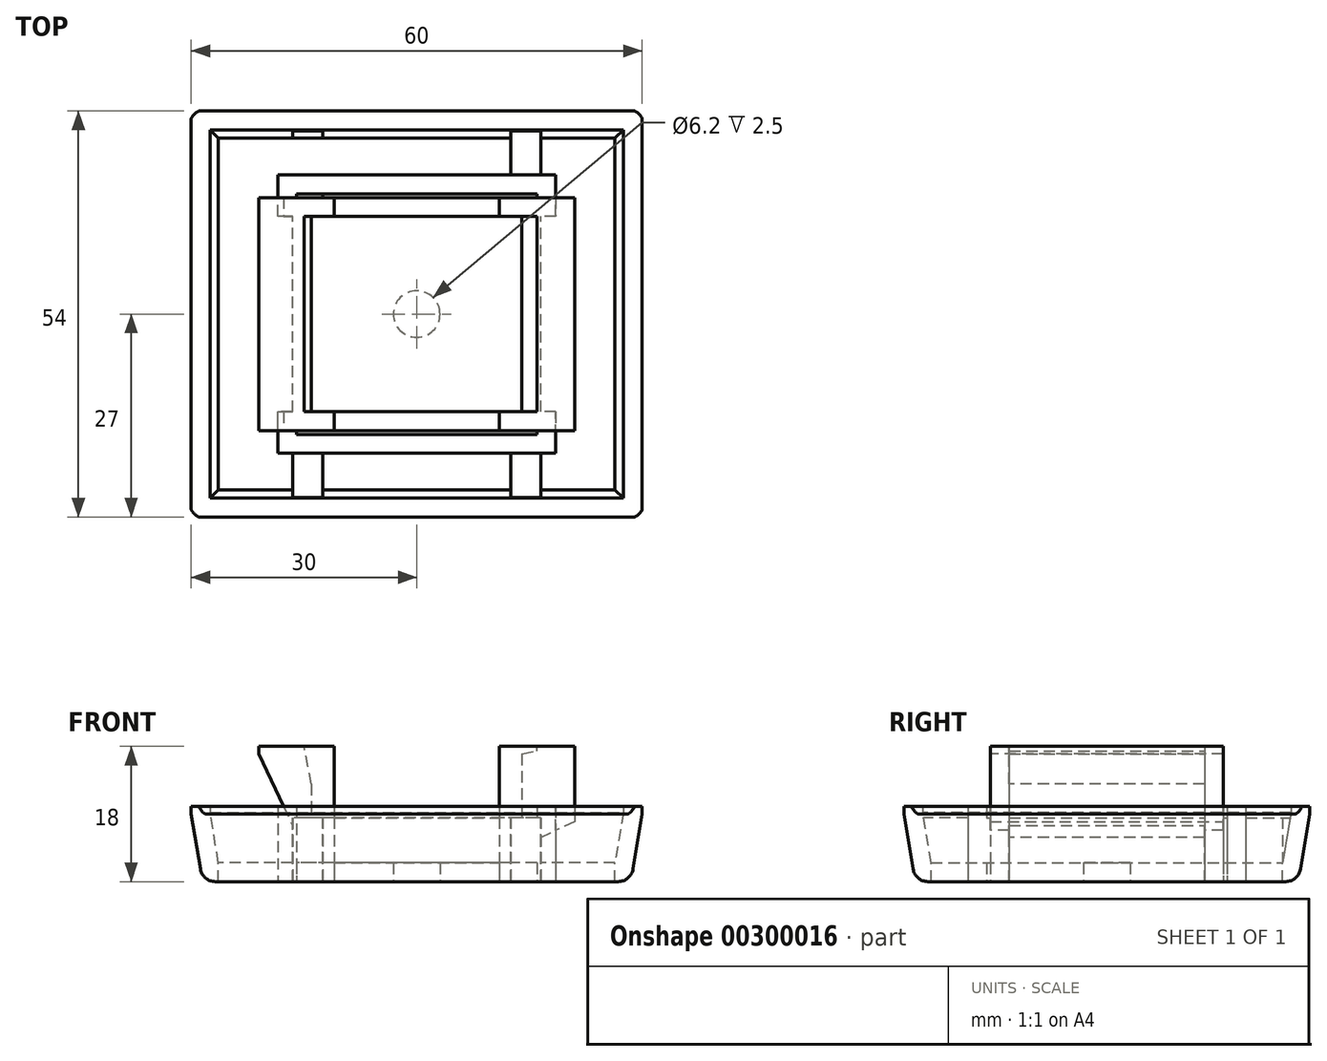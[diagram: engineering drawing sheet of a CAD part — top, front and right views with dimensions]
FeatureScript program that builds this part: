
annotation { "Feature Type Name" : "Feature", "Feature Type Description" : "" }
export const myFeature = defineFeature(function(context is Context, id is Id, definition is map)
    precondition{}
    {
        {
            var Q0;
            Q0=qCreatedBy(makeId("Top.planeOp"),FACE);
            var sketch = newSketch(context, id + "F0", { "sketchPlane" : qUnion([Q0])});
            skLineSegment(sketch, "E0.bottom", {"start": v(30, -27) * mm, "end": v(-30, -27) * mm});
            skLineSegment(sketch, "E0.top", {"start": v(30, 27) * mm, "end": v(-30, 27) * mm});
            skLineSegment(sketch, "E0.left", {"start": v(30, -27) * mm, "end": v(30, 27) * mm});
            skLineSegment(sketch, "E0.right", {"start": v(-30, -27) * mm, "end": v(-30, 27) * mm});
            skPoint(sketch, "E0.middle", {"position": v(0, 0) * mm});
            skLineSegment(sketch, "E1.bottom", {"start": v(21, -15.5) * mm, "end": v(-21, -15.5) * mm});
            skLineSegment(sketch, "E1.top", {"start": v(21, 15.5) * mm, "end": v(-21, 15.5) * mm});
            skLineSegment(sketch, "E1.left", {"start": v(21, -15.5) * mm, "end": v(21, 15.5) * mm});
            skLineSegment(sketch, "E1.right", {"start": v(-21, -15.5) * mm, "end": v(-21, 15.5) * mm});
            skCircle(sketch, "E2", {"center": v(0, 0) * mm, "radius": 3.1 * mm});
            skLineSegment(sketch, "E3.bottom", {"start": v(11, -15.5) * mm, "end": v(-11, -15.5) * mm});
            skLineSegment(sketch, "E3.top", {"start": v(11, 15.5) * mm, "end": v(-11, 15.5) * mm});
            skLineSegment(sketch, "E3.left", {"start": v(11, -15.5) * mm, "end": v(11, 15.5) * mm});
            skLineSegment(sketch, "E3.right", {"start": v(-11, -15.5) * mm, "end": v(-11, 15.5) * mm});
            skLineSegment(sketch, "E4.bottom", {"start": v(14, -13) * mm, "end": v(-14, -13) * mm});
            skLineSegment(sketch, "E4.top", {"start": v(14, 13) * mm, "end": v(-14, 13) * mm});
            skLineSegment(sketch, "E4.left", {"start": v(14, -13) * mm, "end": v(14, 13) * mm});
            skLineSegment(sketch, "E4.right", {"start": v(-14, -13) * mm, "end": v(-14, 13) * mm});
            skLineSegment(sketch, "E5.bottom", {"start": v(16, -16) * mm, "end": v(-16, -16) * mm});
            skLineSegment(sketch, "E5.top", {"start": v(16, 16) * mm, "end": v(-16, 16) * mm});
            skLineSegment(sketch, "E5.left", {"start": v(16, -16) * mm, "end": v(16, 16) * mm});
            skLineSegment(sketch, "E5.right", {"start": v(-16, -16) * mm, "end": v(-16, 16) * mm});
            skSolve(sketch);
        }
        {
            var Q0;
            Q0=makeQuery(id+"F0.imprint","IMPRINT",FACE,{"disambiguationData":[TD([[makeQuery(id+"F0.imprint","IMPRINT",EDGE,{"derivedFrom":sQuery(id+"F0.wireOp",EDGE,"E0.bottom")}),-1.0]])]});
            var Q1;
            {var subQ0=sQuery(id+"F0.wireOp",EDGE,"E3.top");Q1=makeQuery(id+"F0.imprint","IMPRINT",FACE,{"disambiguationData":[TD([[makeQuery(id+"F0.imprint","IMPRINT",EDGE,{"derivedFrom":subQ0}),1.0]])]});}
            var Q2;
            {var subQ0=sQuery(id+"F0.wireOp",EDGE,"E3.bottom");Q2=makeQuery(id+"F0.imprint","IMPRINT",FACE,{"disambiguationData":[TD([[makeQuery(id+"F0.imprint","IMPRINT",EDGE,{"derivedFrom":subQ0}),-1.0]])]});}
            var Q3;
            {var subQ0=sQuery(id+"F0.wireOp",EDGE,"E1.right");Q3=makeQuery(id+"F0.imprint","IMPRINT",FACE,{"disambiguationData":[TD([[makeQuery(id+"F0.imprint","IMPRINT",EDGE,{"derivedFrom":subQ0}),-1.0]])]});}
            var Q4;
            {var subQ0=sQuery(id+"F0.wireOp",EDGE,"E1.left");Q4=makeQuery(id+"F0.imprint","IMPRINT",FACE,{"disambiguationData":[TD([[makeQuery(id+"F0.imprint","IMPRINT",EDGE,{"derivedFrom":subQ0}),1.0]])]});}
            var Q5;
            {var subQ1=sQuery(id+"F0.wireOp",EDGE,"E3.bottom");Q5=makeQuery(id+"F0.imprint","IMPRINT",FACE,{"disambiguationData":[TD([[makeQuery(id+"F0.imprint","IMPRINT",EDGE,{"derivedFrom":subQ1}),1.0]])]});}
            var Q6;
            {var subQ1=sQuery(id+"F0.wireOp",EDGE,"E3.top");Q6=makeQuery(id+"F0.imprint","IMPRINT",FACE,{"disambiguationData":[TD([[makeQuery(id+"F0.imprint","IMPRINT",EDGE,{"derivedFrom":subQ1}),-1.0]])]});}
            extrude(context, id + "F1", {"entities" : qUnion([Q0, Q1, Q2, Q3, Q4, Q5, Q6]), "depth" : 10 * mm});
        }
        {
            var Q0;
            Q0=makeQuery(id+"F0.imprint","IMPRINT",FACE,{"disambiguationData":[TD([[makeQuery(id+"F0.imprint","IMPRINT",EDGE,{"derivedFrom":sQuery(id+"F0.wireOp",EDGE,"E2")}),-1.0]])]});
            var Q1;
            {var subQ5=sQuery(id+"F0.wireOp",EDGE,"E4.right");Q1=makeQuery(id+"F0.imprint","IMPRINT",FACE,{"disambiguationData":[TD([[makeQuery(id+"F0.imprint","IMPRINT",EDGE,{"derivedFrom":subQ5}),-1.0]])]});}
            var Q2;
            {var subQ5=sQuery(id+"F0.wireOp",EDGE,"E4.left");Q2=makeQuery(id+"F0.imprint","IMPRINT",FACE,{"disambiguationData":[TD([[makeQuery(id+"F0.imprint","IMPRINT",EDGE,{"derivedFrom":subQ5}),1.0]])]});}
            extrude(context, id + "F2", {"entities" : qUnion([Q0, Q1, Q2]), "operationType" : NewBodyOperationType.ADD, "depth" : 5 * mm});
        }
        {
            var Q0;
            Q0=makeQuery(id+"F1.opExtrude","CAP_EDGE",EDGE,{"disambiguationData":[OSD([sQuery(id+"F0.wireOp",EDGE,"E0.right")])],"isStart":true});
            var Q1;
            Q1=makeQuery(id+"F1.opExtrude","CAP_EDGE",EDGE,{"disambiguationData":[OSD([sQuery(id+"F0.wireOp",EDGE,"E0.bottom")])],"isStart":true});
            var Q2;
            Q2=makeQuery(id+"F1.opExtrude","CAP_EDGE",EDGE,{"disambiguationData":[OSD([sQuery(id+"F0.wireOp",EDGE,"E0.left")])],"isStart":true});
            var Q3;
            Q3=makeQuery(id+"F1.opExtrude","CAP_EDGE",EDGE,{"disambiguationData":[OSD([sQuery(id+"F0.wireOp",EDGE,"E0.top")])],"isStart":true});
            chamfer(context, id + "F3", {"entities" : qUnion([Q0, Q1, Q2, Q3]), "chamferType" : ChamferType.TWO_OFFSETS, "width1" : 1.5 * mm, "oppositeDirection" : false, "width2" : 9 * mm, "tangentPropagation" : true});
        }
        {
            var Q0;
            {var subQ12=sQuery(id+"F0.wireOp",EDGE,"E4.right");Q0=makeQuery(id+"F0.imprint","IMPRINT",FACE,{"disambiguationData":[TD([[makeQuery(id+"F0.imprint","IMPRINT",EDGE,{"derivedFrom":subQ12}),1.0]])]});}
            var Q1;
            {var subQ12=sQuery(id+"F0.wireOp",EDGE,"E4.left");Q1=makeQuery(id+"F0.imprint","IMPRINT",FACE,{"disambiguationData":[TD([[makeQuery(id+"F0.imprint","IMPRINT",EDGE,{"derivedFrom":subQ12}),-1.0]])]});}
            extrude(context, id + "F4", {"entities" : qUnion([Q0, Q1]), "operationType" : NewBodyOperationType.ADD, "depth" : 18 * mm});
        }
        {
            var Q0;
            Q0=makeQuery(id+"F4.opExtrude","CAP_EDGE",EDGE,{"disambiguationData":[OSD([sQuery(id+"F0.wireOp",EDGE,"E4.right")])],"isStart":false});
            chamfer(context, id + "F5", {"entities" : qUnion([Q0]), "chamferType" : ChamferType.TWO_OFFSETS, "width1" : 1 * mm, "oppositeDirection" : false, "width2" : 5 * mm, "tangentPropagation" : true});
        }
        {
            var Q0;
            Q0=makeQuery(id+"F4.opExtrude","CAP_EDGE",EDGE,{"disambiguationData":[OSD([sQuery(id+"F0.wireOp",EDGE,"E4.left")])],"isStart":false});
            chamfer(context, id + "F6", {"entities" : qUnion([Q0]), "chamferType" : ChamferType.TWO_OFFSETS, "width1" : 5 * mm, "oppositeDirection" : false, "width2" : 1 * mm, "tangentPropagation" : true});
        }
        {
            var Q0;
            {var subQ0=sQuery(id+"F0.wireOp",EDGE,"E1.right");Q0=makeQuery(id+"F0.imprint","IMPRINT",FACE,{"disambiguationData":[TD([[makeQuery(id+"F0.imprint","IMPRINT",EDGE,{"derivedFrom":subQ0}),-1.0]])]});}
            var Q1;
            {var subQ0=sQuery(id+"F0.wireOp",EDGE,"E1.left");Q1=makeQuery(id+"F0.imprint","IMPRINT",FACE,{"disambiguationData":[TD([[makeQuery(id+"F0.imprint","IMPRINT",EDGE,{"derivedFrom":subQ0}),1.0]])]});}
            extrude(context, id + "F7", {"entities" : qUnion([Q0, Q1]), "depth" : 18 * mm});
        }
        {
            var Q0;
            Q0=makeQuery(id+"F7.opExtrude","CAP_EDGE",EDGE,{"disambiguationData":[OSD([sQuery(id+"F0.wireOp",EDGE,"E1.right")])],"isStart":true});
            chamfer(context, id + "F8", {"entities" : qUnion([Q0]), "chamferType" : ChamferType.TWO_OFFSETS, "width1" : 8 * mm, "oppositeDirection" : false, "width2" : 17 * mm, "tangentPropagation" : true});
        }
        {
            var Q0;
            Q0=makeQuery(id+"F7.opExtrude","CAP_EDGE",EDGE,{"disambiguationData":[OSD([sQuery(id+"F0.wireOp",EDGE,"E1.left")])],"isStart":true});
            chamfer(context, id + "F9", {"entities" : qUnion([Q0]), "chamferType" : ChamferType.TWO_OFFSETS, "width1" : 8 * mm, "oppositeDirection" : true, "width2" : 17 * mm, "tangentPropagation" : true});
        }
        {
            var Q0;
            Q0=makeQuery(id+"F1.opExtrude","CAP_FACE",FACE,{"disambiguationData":[OSD([sQuery(id+"F0.wireOp",EDGE,"E0.bottom"),sQuery(id+"F0.wireOp",EDGE,"E0.top"),sQuery(id+"F0.wireOp",EDGE,"E0.left"),sQuery(id+"F0.wireOp",EDGE,"E0.right"),sQuery(id+"F0.wireOp",EDGE,"E1.bottom"),sQuery(id+"F0.wireOp",EDGE,"E1.top"),sQuery(id+"F0.wireOp",EDGE,"E3.left"),sQuery(id+"F0.wireOp",EDGE,"E3.right"),sQuery(id+"F0.wireOp",EDGE,"E4.bottom"),sQuery(id+"F0.wireOp",EDGE,"E4.top"),sQuery(id+"F0.wireOp",EDGE,"E5.left"),sQuery(id+"F0.wireOp",EDGE,"E5.right")])],"isStart":false});
            shell(context, id + "F10", {"entities" : qUnion([Q0]), "thickness" : 2.5 * mm});
        }
        {
            var Q0;
            Q0=makeQuery(id+"F3.opChamfer","BLEND_EDGE",EDGE,{"blendedFrom":[makeQuery(id+"F1.opExtrude","CAP_EDGE",EDGE,{"disambiguationData":[OSD([sQuery(id+"F0.wireOp",EDGE,"E0.bottom")])],"isStart":true}),makeQuery(id+"F1.opExtrude","CAP_EDGE",EDGE,{"disambiguationData":[OSD([sQuery(id+"F0.wireOp",EDGE,"E0.right")])],"isStart":true})],"blendedInto":[]});
            var Q1;
            Q1=makeQuery(id+"F3.opChamfer","BLEND_EDGE",EDGE,{"blendedFrom":[makeQuery(id+"F1.opExtrude","CAP_EDGE",EDGE,{"disambiguationData":[OSD([sQuery(id+"F0.wireOp",EDGE,"E0.top")])],"isStart":true}),makeQuery(id+"F1.opExtrude","CAP_EDGE",EDGE,{"disambiguationData":[OSD([sQuery(id+"F0.wireOp",EDGE,"E0.right")])],"isStart":true})],"blendedInto":[]});
            var Q2;
            Q2=makeQuery(id+"F3.opChamfer","BLEND_EDGE",EDGE,{"blendedFrom":[makeQuery(id+"F1.opExtrude","CAP_EDGE",EDGE,{"disambiguationData":[OSD([sQuery(id+"F0.wireOp",EDGE,"E0.top")])],"isStart":true}),makeQuery(id+"F1.opExtrude","CAP_EDGE",EDGE,{"disambiguationData":[OSD([sQuery(id+"F0.wireOp",EDGE,"E0.left")])],"isStart":true})],"blendedInto":[]});
            var Q3;
            Q3=makeQuery(id+"F3.opChamfer","BLEND_EDGE",EDGE,{"blendedFrom":[makeQuery(id+"F1.opExtrude","CAP_EDGE",EDGE,{"disambiguationData":[OSD([sQuery(id+"F0.wireOp",EDGE,"E0.bottom")])],"isStart":true}),makeQuery(id+"F1.opExtrude","CAP_EDGE",EDGE,{"disambiguationData":[OSD([sQuery(id+"F0.wireOp",EDGE,"E0.left")])],"isStart":true})],"blendedInto":[]});
            var Q4;
            {var subQ0=sQuery(id+"F0.wireOp",EDGE,"E4.top");var subQ1=sQuery(id+"F0.wireOp",EDGE,"E4.bottom");var subQ2=sQuery(id+"F0.wireOp",EDGE,"E0.left");Q4=makeQuery(id+"F3.opChamfer","BLEND_EDGE",EDGE,{"blendedFrom":[makeQuery(id+"F1.opExtrude","CAP_EDGE",EDGE,{"disambiguationData":[OSD([subQ2])],"isStart":true}),makeQuery(id+"F2.boolean.opBoolean","MERGE",FACE,{"derivedFrom":[makeQuery(id+"F1.opExtrude","CAP_FACE",FACE,{"disambiguationData":[OSD([sQuery(id+"F0.wireOp",EDGE,"E0.bottom"),sQuery(id+"F0.wireOp",EDGE,"E0.top"),subQ2,sQuery(id+"F0.wireOp",EDGE,"E0.right"),sQuery(id+"F0.wireOp",EDGE,"E1.bottom"),sQuery(id+"F0.wireOp",EDGE,"E1.top"),sQuery(id+"F0.wireOp",EDGE,"E3.left"),sQuery(id+"F0.wireOp",EDGE,"E3.right"),subQ1,subQ0,sQuery(id+"F0.wireOp",EDGE,"E5.left"),sQuery(id+"F0.wireOp",EDGE,"E5.right")])],"isStart":true}),makeQuery(id+"F2.opExtrude","CAP_FACE",FACE,{"disambiguationData":[OSD([sQuery(id+"F0.wireOp",EDGE,"E2"),subQ1,subQ0,sQuery(id+"F0.wireOp",EDGE,"E4.left"),sQuery(id+"F0.wireOp",EDGE,"E4.right")])],"isStart":true})]})],"blendedInto":[makeQuery(id+"F2.boolean.opBoolean","MERGE",FACE,{"derivedFrom":[makeQuery(id+"F1.opExtrude","CAP_FACE",FACE,{"disambiguationData":[OSD([sQuery(id+"F0.wireOp",EDGE,"E0.bottom"),sQuery(id+"F0.wireOp",EDGE,"E0.top"),subQ2,sQuery(id+"F0.wireOp",EDGE,"E0.right"),sQuery(id+"F0.wireOp",EDGE,"E1.bottom"),sQuery(id+"F0.wireOp",EDGE,"E1.top"),sQuery(id+"F0.wireOp",EDGE,"E3.left"),sQuery(id+"F0.wireOp",EDGE,"E3.right"),subQ1,subQ0,sQuery(id+"F0.wireOp",EDGE,"E5.left"),sQuery(id+"F0.wireOp",EDGE,"E5.right")])],"isStart":true}),makeQuery(id+"F2.opExtrude","CAP_FACE",FACE,{"disambiguationData":[OSD([sQuery(id+"F0.wireOp",EDGE,"E2"),subQ1,subQ0,sQuery(id+"F0.wireOp",EDGE,"E4.left"),sQuery(id+"F0.wireOp",EDGE,"E4.right")])],"isStart":true})]})]});}
            var Q5;
            {var subQ0=sQuery(id+"F0.wireOp",EDGE,"E4.top");var subQ1=sQuery(id+"F0.wireOp",EDGE,"E4.bottom");var subQ2=sQuery(id+"F0.wireOp",EDGE,"E0.bottom");Q5=makeQuery(id+"F3.opChamfer","BLEND_EDGE",EDGE,{"blendedFrom":[makeQuery(id+"F1.opExtrude","CAP_EDGE",EDGE,{"disambiguationData":[OSD([subQ2])],"isStart":true}),makeQuery(id+"F2.boolean.opBoolean","MERGE",FACE,{"derivedFrom":[makeQuery(id+"F1.opExtrude","CAP_FACE",FACE,{"disambiguationData":[OSD([subQ2,sQuery(id+"F0.wireOp",EDGE,"E0.top"),sQuery(id+"F0.wireOp",EDGE,"E0.left"),sQuery(id+"F0.wireOp",EDGE,"E0.right"),sQuery(id+"F0.wireOp",EDGE,"E1.bottom"),sQuery(id+"F0.wireOp",EDGE,"E1.top"),sQuery(id+"F0.wireOp",EDGE,"E3.left"),sQuery(id+"F0.wireOp",EDGE,"E3.right"),subQ1,subQ0,sQuery(id+"F0.wireOp",EDGE,"E5.left"),sQuery(id+"F0.wireOp",EDGE,"E5.right")])],"isStart":true}),makeQuery(id+"F2.opExtrude","CAP_FACE",FACE,{"disambiguationData":[OSD([sQuery(id+"F0.wireOp",EDGE,"E2"),subQ1,subQ0,sQuery(id+"F0.wireOp",EDGE,"E4.left"),sQuery(id+"F0.wireOp",EDGE,"E4.right")])],"isStart":true})]})],"blendedInto":[makeQuery(id+"F2.boolean.opBoolean","MERGE",FACE,{"derivedFrom":[makeQuery(id+"F1.opExtrude","CAP_FACE",FACE,{"disambiguationData":[OSD([subQ2,sQuery(id+"F0.wireOp",EDGE,"E0.top"),sQuery(id+"F0.wireOp",EDGE,"E0.left"),sQuery(id+"F0.wireOp",EDGE,"E0.right"),sQuery(id+"F0.wireOp",EDGE,"E1.bottom"),sQuery(id+"F0.wireOp",EDGE,"E1.top"),sQuery(id+"F0.wireOp",EDGE,"E3.left"),sQuery(id+"F0.wireOp",EDGE,"E3.right"),subQ1,subQ0,sQuery(id+"F0.wireOp",EDGE,"E5.left"),sQuery(id+"F0.wireOp",EDGE,"E5.right")])],"isStart":true}),makeQuery(id+"F2.opExtrude","CAP_FACE",FACE,{"disambiguationData":[OSD([sQuery(id+"F0.wireOp",EDGE,"E2"),subQ1,subQ0,sQuery(id+"F0.wireOp",EDGE,"E4.left"),sQuery(id+"F0.wireOp",EDGE,"E4.right")])],"isStart":true})]})]});}
            var Q6;
            {var subQ0=sQuery(id+"F0.wireOp",EDGE,"E4.top");var subQ1=sQuery(id+"F0.wireOp",EDGE,"E4.bottom");var subQ2=sQuery(id+"F0.wireOp",EDGE,"E0.right");Q6=makeQuery(id+"F3.opChamfer","BLEND_EDGE",EDGE,{"blendedFrom":[makeQuery(id+"F1.opExtrude","CAP_EDGE",EDGE,{"disambiguationData":[OSD([subQ2])],"isStart":true}),makeQuery(id+"F2.boolean.opBoolean","MERGE",FACE,{"derivedFrom":[makeQuery(id+"F1.opExtrude","CAP_FACE",FACE,{"disambiguationData":[OSD([sQuery(id+"F0.wireOp",EDGE,"E0.bottom"),sQuery(id+"F0.wireOp",EDGE,"E0.top"),sQuery(id+"F0.wireOp",EDGE,"E0.left"),subQ2,sQuery(id+"F0.wireOp",EDGE,"E1.bottom"),sQuery(id+"F0.wireOp",EDGE,"E1.top"),sQuery(id+"F0.wireOp",EDGE,"E3.left"),sQuery(id+"F0.wireOp",EDGE,"E3.right"),subQ1,subQ0,sQuery(id+"F0.wireOp",EDGE,"E5.left"),sQuery(id+"F0.wireOp",EDGE,"E5.right")])],"isStart":true}),makeQuery(id+"F2.opExtrude","CAP_FACE",FACE,{"disambiguationData":[OSD([sQuery(id+"F0.wireOp",EDGE,"E2"),subQ1,subQ0,sQuery(id+"F0.wireOp",EDGE,"E4.left"),sQuery(id+"F0.wireOp",EDGE,"E4.right")])],"isStart":true})]})],"blendedInto":[makeQuery(id+"F2.boolean.opBoolean","MERGE",FACE,{"derivedFrom":[makeQuery(id+"F1.opExtrude","CAP_FACE",FACE,{"disambiguationData":[OSD([sQuery(id+"F0.wireOp",EDGE,"E0.bottom"),sQuery(id+"F0.wireOp",EDGE,"E0.top"),sQuery(id+"F0.wireOp",EDGE,"E0.left"),subQ2,sQuery(id+"F0.wireOp",EDGE,"E1.bottom"),sQuery(id+"F0.wireOp",EDGE,"E1.top"),sQuery(id+"F0.wireOp",EDGE,"E3.left"),sQuery(id+"F0.wireOp",EDGE,"E3.right"),subQ1,subQ0,sQuery(id+"F0.wireOp",EDGE,"E5.left"),sQuery(id+"F0.wireOp",EDGE,"E5.right")])],"isStart":true}),makeQuery(id+"F2.opExtrude","CAP_FACE",FACE,{"disambiguationData":[OSD([sQuery(id+"F0.wireOp",EDGE,"E2"),subQ1,subQ0,sQuery(id+"F0.wireOp",EDGE,"E4.left"),sQuery(id+"F0.wireOp",EDGE,"E4.right")])],"isStart":true})]})]});}
            var Q7;
            {var subQ0=sQuery(id+"F0.wireOp",EDGE,"E4.top");var subQ1=sQuery(id+"F0.wireOp",EDGE,"E4.bottom");var subQ2=sQuery(id+"F0.wireOp",EDGE,"E0.top");Q7=makeQuery(id+"F3.opChamfer","BLEND_EDGE",EDGE,{"blendedFrom":[makeQuery(id+"F1.opExtrude","CAP_EDGE",EDGE,{"disambiguationData":[OSD([subQ2])],"isStart":true}),makeQuery(id+"F2.boolean.opBoolean","MERGE",FACE,{"derivedFrom":[makeQuery(id+"F1.opExtrude","CAP_FACE",FACE,{"disambiguationData":[OSD([sQuery(id+"F0.wireOp",EDGE,"E0.bottom"),subQ2,sQuery(id+"F0.wireOp",EDGE,"E0.left"),sQuery(id+"F0.wireOp",EDGE,"E0.right"),sQuery(id+"F0.wireOp",EDGE,"E1.bottom"),sQuery(id+"F0.wireOp",EDGE,"E1.top"),sQuery(id+"F0.wireOp",EDGE,"E3.left"),sQuery(id+"F0.wireOp",EDGE,"E3.right"),subQ1,subQ0,sQuery(id+"F0.wireOp",EDGE,"E5.left"),sQuery(id+"F0.wireOp",EDGE,"E5.right")])],"isStart":true}),makeQuery(id+"F2.opExtrude","CAP_FACE",FACE,{"disambiguationData":[OSD([sQuery(id+"F0.wireOp",EDGE,"E2"),subQ1,subQ0,sQuery(id+"F0.wireOp",EDGE,"E4.left"),sQuery(id+"F0.wireOp",EDGE,"E4.right")])],"isStart":true})]})],"blendedInto":[makeQuery(id+"F2.boolean.opBoolean","MERGE",FACE,{"derivedFrom":[makeQuery(id+"F1.opExtrude","CAP_FACE",FACE,{"disambiguationData":[OSD([sQuery(id+"F0.wireOp",EDGE,"E0.bottom"),subQ2,sQuery(id+"F0.wireOp",EDGE,"E0.left"),sQuery(id+"F0.wireOp",EDGE,"E0.right"),sQuery(id+"F0.wireOp",EDGE,"E1.bottom"),sQuery(id+"F0.wireOp",EDGE,"E1.top"),sQuery(id+"F0.wireOp",EDGE,"E3.left"),sQuery(id+"F0.wireOp",EDGE,"E3.right"),subQ1,subQ0,sQuery(id+"F0.wireOp",EDGE,"E5.left"),sQuery(id+"F0.wireOp",EDGE,"E5.right")])],"isStart":true}),makeQuery(id+"F2.opExtrude","CAP_FACE",FACE,{"disambiguationData":[OSD([sQuery(id+"F0.wireOp",EDGE,"E2"),subQ1,subQ0,sQuery(id+"F0.wireOp",EDGE,"E4.left"),sQuery(id+"F0.wireOp",EDGE,"E4.right")])],"isStart":true})]})]});}
            fillet(context, id + "F11", {"entities" : qUnion([Q0, Q1, Q2, Q3, Q4, Q5, Q6, Q7]), "radius" : 2 * mm, "tangentPropagation" : true, "allowEdgeOverflow" : false});
        }
        {
            var Q0;
            Q0=makeQuery(id+"F10.opShell","OFFSET_FACE",FACE,{"disambiguationData":[OSD([sQuery(id+"F0.wireOp",EDGE,"E0.bottom"),sQuery(id+"F0.wireOp",EDGE,"E0.top"),sQuery(id+"F0.wireOp",EDGE,"E0.left"),sQuery(id+"F0.wireOp",EDGE,"E0.right"),sQuery(id+"F0.wireOp",EDGE,"E1.bottom"),sQuery(id+"F0.wireOp",EDGE,"E1.top"),sQuery(id+"F0.wireOp",EDGE,"E2"),sQuery(id+"F0.wireOp",EDGE,"E3.left"),sQuery(id+"F0.wireOp",EDGE,"E3.right"),sQuery(id+"F0.wireOp",EDGE,"E4.bottom"),sQuery(id+"F0.wireOp",EDGE,"E4.top"),sQuery(id+"F0.wireOp",EDGE,"E4.left"),sQuery(id+"F0.wireOp",EDGE,"E4.right"),sQuery(id+"F0.wireOp",EDGE,"E5.left"),sQuery(id+"F0.wireOp",EDGE,"E5.right")])]});
            var sketch = newSketch(context, id + "F12", { "sketchPlane" : qUnion([Q0])});
            skLineSegment(sketch, "E6.bottom", {"start": v(-16.5, 15.5) * mm, "end": v(-12.5, 15.5) * mm});
            skLineSegment(sketch, "E6.left", {"start": v(-16.5, 15.5) * mm, "end": v(-16.5, 25) * mm});
            skLineSegment(sketch, "E6.right", {"start": v(-12.5, 15.5) * mm, "end": v(-12.5, 25) * mm});
            skLineSegment(sketch, "E7.bottom", {"start": v(-11, 13) * mm, "end": v(0, 13) * mm});
            skLineSegment(sketch, "E7.top", {"start": v(-11, 15.5) * mm, "end": v(0, 15.5) * mm});
            skLineSegment(sketch, "E7.left", {"start": v(-11, 13) * mm, "end": v(-11, 15.5) * mm});
            skLineSegment(sketch, "E7.right", {"start": v(0, 13) * mm, "end": v(0, 15.5) * mm});
            skLineSegment(sketch, "E8.MirrorCS", {"start": v(12.5, 15.5) * mm, "end": v(12.5, 25) * mm});
            skLineSegment(sketch, "E9.MirrorCS", {"start": v(17.5, 25) * mm, "end": v(12.5, 25) * mm});
            skLineSegment(sketch, "E10.MirrorCS", {"start": v(16.5, 15.5) * mm, "end": v(16.5, 25) * mm});
            skLineSegment(sketch, "E11.MirrorCS", {"start": v(16.5, 15.5) * mm, "end": v(12.5, 15.5) * mm});
            skLineSegment(sketch, "E12.MirrorCS", {"start": v(11, 15.5) * mm, "end": v(0, 15.5) * mm});
            skLineSegment(sketch, "E13.MirrorCS", {"start": v(11, 13) * mm, "end": v(11, 15.5) * mm});
            skLineSegment(sketch, "E14.MirrorCS", {"start": v(11, 13) * mm, "end": v(0, 13) * mm});
            skLineSegment(sketch, "E15.MirrorCS", {"start": v(-16.5, -15.5) * mm, "end": v(-16.5, -25) * mm});
            skLineSegment(sketch, "E16.MirrorCS", {"start": v(-17.5, -25) * mm, "end": v(-12.5, -25) * mm});
            skLineSegment(sketch, "E17.MirrorCS", {"start": v(-12.5, -15.5) * mm, "end": v(-12.5, -25) * mm});
            skLineSegment(sketch, "E18.MirrorCS", {"start": v(-16.5, -15.5) * mm, "end": v(-12.5, -15.5) * mm});
            skLineSegment(sketch, "E19.MirrorCS", {"start": v(-11, -13) * mm, "end": v(-11, -15.5) * mm});
            skLineSegment(sketch, "E20.MirrorCS", {"start": v(-11, -15.5) * mm, "end": v(0, -15.5) * mm});
            skLineSegment(sketch, "E21.MirrorCS", {"start": v(-11, -13) * mm, "end": v(0, -13) * mm});
            skLineSegment(sketch, "E22.MirrorCS", {"start": v(11, -13) * mm, "end": v(0, -13) * mm});
            skLineSegment(sketch, "E23.MirrorCS", {"start": v(11, -15.5) * mm, "end": v(0, -15.5) * mm});
            skLineSegment(sketch, "E24.MirrorCS", {"start": v(11, -13) * mm, "end": v(11, -15.5) * mm});
            skLineSegment(sketch, "E25.MirrorCS", {"start": v(12.5, -15.5) * mm, "end": v(12.5, -25) * mm});
            skLineSegment(sketch, "E26.MirrorCS", {"start": v(16.5, -15.5) * mm, "end": v(12.5, -15.5) * mm});
            skLineSegment(sketch, "E27.MirrorCS", {"start": v(16.5, -15.5) * mm, "end": v(16.5, -25) * mm});
            skLineSegment(sketch, "E28.MirrorCS", {"start": v(17.5, -25) * mm, "end": v(12.5, -25) * mm});
            skLineSegment(sketch, "E29", {"start": v(-16.5, 25) * mm, "end": v(-12.5, 25) * mm});
            skSolve(sketch);
        }
        {
            var Q0;
            Q0=makeQuery(id+"F12.imprint","IMPRINT",FACE,{"disambiguationData":[TD([[makeQuery(id+"F12.imprint","IMPRINT",EDGE,{"derivedFrom":sQuery(id+"F12.wireOp",EDGE,"E6.bottom")}),-1.0]])]});
            var Q1;
            Q1=makeQuery(id+"F12.imprint","IMPRINT",FACE,{"disambiguationData":[TD([[makeQuery(id+"F12.imprint","IMPRINT",EDGE,{"derivedFrom":sQuery(id+"F12.wireOp",EDGE,"E8.MirrorCS")}),-1.0]])]});
            var Q2;
            Q2=makeQuery(id+"F12.imprint","IMPRINT",FACE,{"disambiguationData":[TD([[makeQuery(id+"F12.imprint","IMPRINT",EDGE,{"derivedFrom":sQuery(id+"F12.wireOp",EDGE,"E25.MirrorCS")}),1.0]])]});
            var Q3;
            Q3=makeQuery(id+"F12.imprint","IMPRINT",FACE,{"disambiguationData":[TD([[makeQuery(id+"F12.imprint","IMPRINT",EDGE,{"derivedFrom":sQuery(id+"F12.wireOp",EDGE,"E15.MirrorCS")}),1.0]])]});
            var Q4;
            {var subQ0=sQuery(id+"F12.wireOp",EDGE,"E29");Q4=makeQuery(id+"F12.imprint","IMPRINT",FACE,{"disambiguationData":[TD([[makeQuery(id+"F12.imprint","IMPRINT",EDGE,{"derivedFrom":subQ0}),-1.0]])]});}
            extrude(context, id + "F13", {"entities" : qUnion([Q0, Q1, Q2, Q3, Q4]), "operationType" : NewBodyOperationType.ADD, "depth" : 6 * mm});
        }
        {
            var Q0;
            Q0=makeQuery(id+"F10.opShell","OFFSET_FACE",FACE,{"disambiguationData":[OSD([sQuery(id+"F0.wireOp",EDGE,"E0.bottom"),sQuery(id+"F0.wireOp",EDGE,"E0.top"),sQuery(id+"F0.wireOp",EDGE,"E0.left"),sQuery(id+"F0.wireOp",EDGE,"E0.right"),sQuery(id+"F0.wireOp",EDGE,"E1.bottom"),sQuery(id+"F0.wireOp",EDGE,"E1.top"),sQuery(id+"F0.wireOp",EDGE,"E3.left"),sQuery(id+"F0.wireOp",EDGE,"E3.right"),sQuery(id+"F0.wireOp",EDGE,"E4.bottom"),sQuery(id+"F0.wireOp",EDGE,"E4.top"),sQuery(id+"F0.wireOp",EDGE,"E5.left"),sQuery(id+"F0.wireOp",EDGE,"E5.right")]),OD(2.0)]});
            var Q1;
            Q1=makeQuery(id+"F10.opShell","OFFSET_FACE",FACE,{"disambiguationData":[OSD([sQuery(id+"F0.wireOp",EDGE,"E0.bottom"),sQuery(id+"F0.wireOp",EDGE,"E0.top"),sQuery(id+"F0.wireOp",EDGE,"E0.left"),sQuery(id+"F0.wireOp",EDGE,"E0.right"),sQuery(id+"F0.wireOp",EDGE,"E1.bottom"),sQuery(id+"F0.wireOp",EDGE,"E1.top"),sQuery(id+"F0.wireOp",EDGE,"E3.left"),sQuery(id+"F0.wireOp",EDGE,"E3.right"),sQuery(id+"F0.wireOp",EDGE,"E4.bottom"),sQuery(id+"F0.wireOp",EDGE,"E4.top"),sQuery(id+"F0.wireOp",EDGE,"E5.left"),sQuery(id+"F0.wireOp",EDGE,"E5.right")]),OD(1.0)]});
            extrude(context, id + "F14", {"entities" : qUnion([Q0, Q1]), "operationType" : NewBodyOperationType.REMOVE, "oppositeDirection" : true, "depth" : 5 * mm});
        }
    });
